# Revit family: Haworth_Bac_Table_Round
name_source: partatom
category: Furniture
revit_build: Autodesk Revit 2018 (Build: 20170223_1515(x64)
units: mm (PartAtom-declared; Revit-internal decimal feet)

## family parameters
Always vertical = Yes
Cut with Voids When Loaded = No
OmniClass Number = 23.40.70.14.64.21
OmniClass Title = Systems Furniture
Room Calculation Point = No
Shared = No
Work Plane-Based = No

## types (1)
- HCCE-BCTR - 49dia
    Actual Depth = 49"
    Actual Height = 29"
    Actual Width = 49"
    Assembly Code = E2020200
    Description = Haworth Bac Table Round - 49dia
    Leg Depth = 3 15/16"
    Manufacturer = Haworth
    Model = HCCE-BCTR
    Radius = 24 1/2"
    Revision Number = 4
    Size = Verify Final Dim. w/ Haworth
    Standard Depths = 49 in.
    Standard Height = 29 in.
    Support Depth = 2 93/256"
    Support Height = 4 43/256"
    Table Thickness = 1"
    URL = http://www.haworth.com
    URL - Product = https://www.haworth.com
    Warranty = http://www.haworth.com

## geometry (parser evidence)
native form markers: Sweep x2
no freeform markers — native parametric forms only
